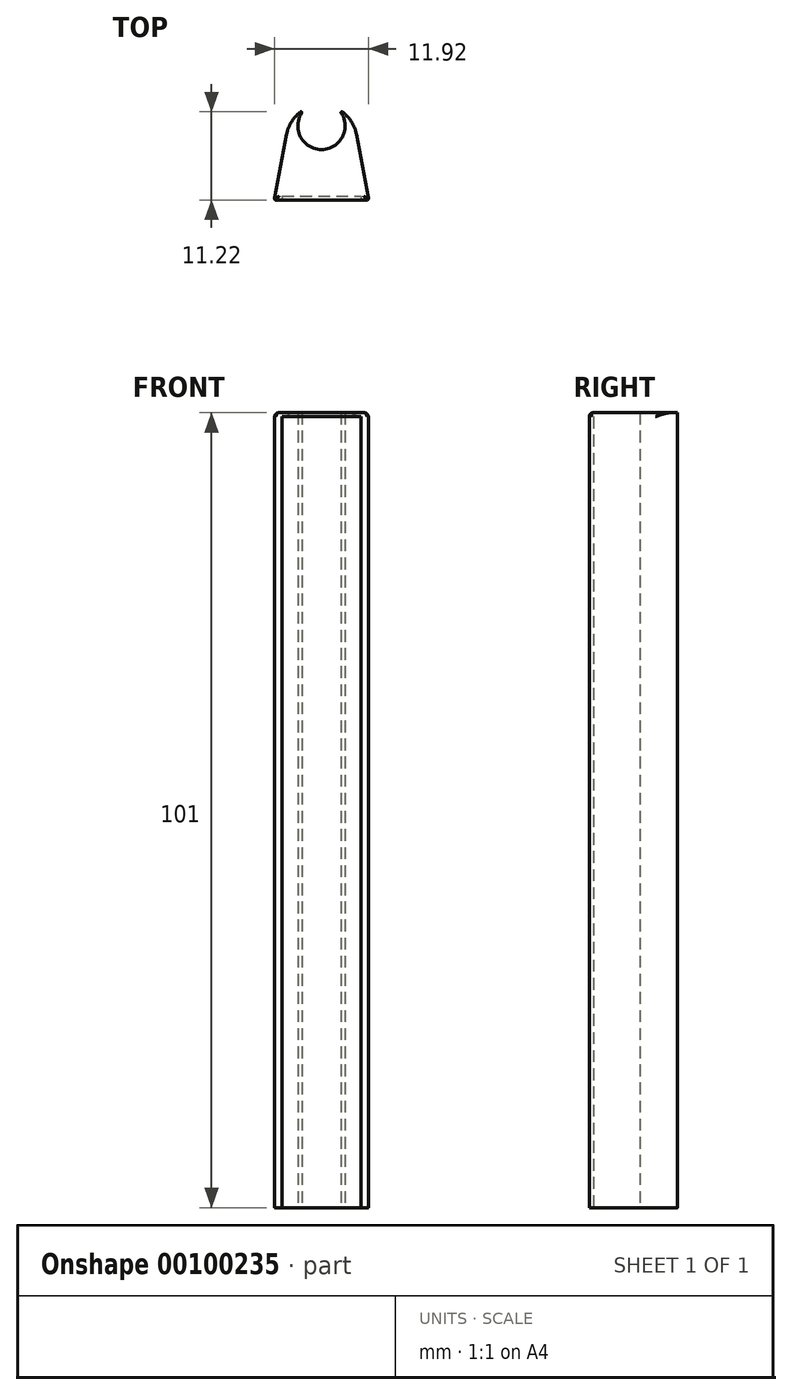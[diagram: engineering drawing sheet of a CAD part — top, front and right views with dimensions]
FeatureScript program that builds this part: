
annotation { "Feature Type Name" : "Feature", "Feature Type Description" : "" }
export const myFeature = defineFeature(function(context is Context, id is Id, definition is map)
    precondition{}
    {
        {
            var Q0;
            Q0=qCreatedBy(makeId("Top.planeOp"),FACE);
            var sketch = newSketch(context, id + "F0", { "sketchPlane" : qUnion([Q0])});
            skArc(sketch, "E0", {"start": v(-2.66, 3.63) * mm, "mid": v(-3.8, 2.4) * mm, "end": v(-4.42, 0.83) * mm});
            skLineSegment(sketch, "E1", {"start": v(0, 5.37) * mm, "end": v(0, -9.74) * mm, "construction": true});
            skLineSegment(sketch, "E2", {"start": v(-5.96, -7.34) * mm, "end": v(-4.42, 0.83) * mm});
            skLineSegment(sketch, "E3", {"start": v(5.96, -7.34) * mm, "end": v(4.42, 0.83) * mm});
            skArc(sketch, "E4", {"start": v(-2.52, 3.5) * mm, "mid": v(0, -1.14) * mm, "end": v(2.52, 3.5) * mm});
            skLineSegment(sketch, "E5", {"start": v(-2.5, 3.45) * mm, "end": v(-2.5, 2.27) * mm, "construction": true});
            skLineSegment(sketch, "E6", {"start": v(2.5, 3.44) * mm, "end": v(2.5, 2.26) * mm, "construction": true});
            skArc(sketch, "E7.filletArc", {"start": v(-2.52, 3.5) * mm, "mid": v(-2.53, 3.62) * mm, "end": v(-2.66, 3.63) * mm});
            skArc(sketch, "E8.filletArc", {"start": v(2.66, 3.63) * mm, "mid": v(2.53, 3.62) * mm, "end": v(2.52, 3.5) * mm});
            skLineSegment(sketch, "E9", {"start": v(-5.76, -7.57) * mm, "end": v(0, -7.57) * mm});
            skLineSegment(sketch, "E10", {"start": v(5.76, -7.57) * mm, "end": v(0, -7.57) * mm});
            skPoint(sketch, "E11.visualSharp", {"position": v(-6, -7.57) * mm});
            skArc(sketch, "E11.filletArc", {"start": v(-5.96, -7.34) * mm, "mid": v(-5.91, -7.5) * mm, "end": v(-5.76, -7.57) * mm});
            skPoint(sketch, "E12.visualSharp", {"position": v(6, -7.57) * mm});
            skArc(sketch, "E12.filletArc", {"start": v(5.76, -7.57) * mm, "mid": v(5.91, -7.5) * mm, "end": v(5.96, -7.34) * mm});
            skArc(sketch, "E13.trimOffspring", {"start": v(4.42, 0.83) * mm, "mid": v(3.8, 2.4) * mm, "end": v(2.66, 3.63) * mm});
            skSolve(sketch);
        }
        {
            var Q0;
            Q0=makeQuery(id+"F0.imprint","IMPRINT",FACE,{"disambiguationData":[TD([[makeQuery(id+"F0.imprint","IMPRINT",EDGE,{"derivedFrom":sQuery(id+"F0.wireOp",EDGE,"E0")}),1.0]])]});
            extrude(context, id + "F1", {"entities" : qUnion([Q0]), "depth" : 101 * mm});
        }
        {
            var Q0;
            Q0=makeQuery(id+"F1.opExtrude","CAP_EDGE",EDGE,{"disambiguationData":[OSD([sQuery(id+"F0.wireOp",EDGE,"E9"),sQuery(id+"F0.wireOp",EDGE,"E10")])],"isStart":false});
            var Q1;
            Q1=makeQuery(id+"F1.opExtrude","CAP_EDGE",EDGE,{"disambiguationData":[OSD([sQuery(id+"F0.wireOp",EDGE,"E2")])],"isStart":false});
            var Q2;
            Q2=makeQuery(id+"F1.opExtrude","CAP_EDGE",EDGE,{"disambiguationData":[OSD([sQuery(id+"F0.wireOp",EDGE,"E3")])],"isStart":false});
            fillet(context, id + "F2", {"entities" : qUnion([Q0, Q1, Q2]), "radius" : 0.5 * mm, "allowEdgeOverflow" : false});
        }
        {
            var Q0;
            Q0=makeQuery(id+"F1.opExtrude","SWEPT_BODY",BODY,{"disambiguationData":[OSD([sQuery(id+"F0.wireOp",EDGE,"E0"),sQuery(id+"F0.wireOp",EDGE,"E2"),sQuery(id+"F0.wireOp",EDGE,"E3"),sQuery(id+"F0.wireOp",EDGE,"E4"),sQuery(id+"F0.wireOp",EDGE,"E7.filletArc"),sQuery(id+"F0.wireOp",EDGE,"E8.filletArc"),sQuery(id+"F0.wireOp",EDGE,"E9"),sQuery(id+"F0.wireOp",EDGE,"E10"),sQuery(id+"F0.wireOp",EDGE,"E11.filletArc"),sQuery(id+"F0.wireOp",EDGE,"E12.filletArc"),sQuery(id+"F0.wireOp",EDGE,"E13.trimOffspring")])]});
            transform(context, id + "F3", {"entities" : qUnion([Q0]), "transformType" : TransformType.TRANSLATION_3D, "dx" : 0 * mm, "dy" : 0 * mm, "dz" : -50.5 * mm, "makeCopy" : false});
        }
        {
            var Q0;
            Q0=makeQuery(id+"F1.opExtrude","SWEPT_FACE",FACE,{"disambiguationData":[OSD([sQuery(id+"F0.wireOp",EDGE,"E9"),sQuery(id+"F0.wireOp",EDGE,"E10")])]});
            var sketch = newSketch(context, id + "F4", { "sketchPlane" : qUnion([Q0])});
            skLineSegment(sketch, "E14.bottom", {"start": v(-5, 50) * mm, "end": v(5, 50) * mm});
            skLineSegment(sketch, "E14.top", {"start": v(-5, -50.5) * mm, "end": v(5, -50.5) * mm});
            skLineSegment(sketch, "E14.left", {"start": v(-5, 50) * mm, "end": v(-5, -50.5) * mm});
            skLineSegment(sketch, "E14.right", {"start": v(5, 50) * mm, "end": v(5, -50.5) * mm});
            skLineSegment(sketch, "E15", {"start": v(-5.76, 0) * mm, "end": v(-5, 0) * mm, "construction": true});
            skLineSegment(sketch, "E16", {"start": v(5, 0) * mm, "end": v(5.76, 0) * mm, "construction": true});
            skSolve(sketch);
        }
        {
            var Q0;
            Q0 = qSketchRegion(id + "F4", true);
            extrude(context, id + "F5", {"entities" : qUnion([Q0]), "operationType" : NewBodyOperationType.REMOVE, "oppositeDirection" : true, "depth" : 0.5 * mm});
        }
    });
